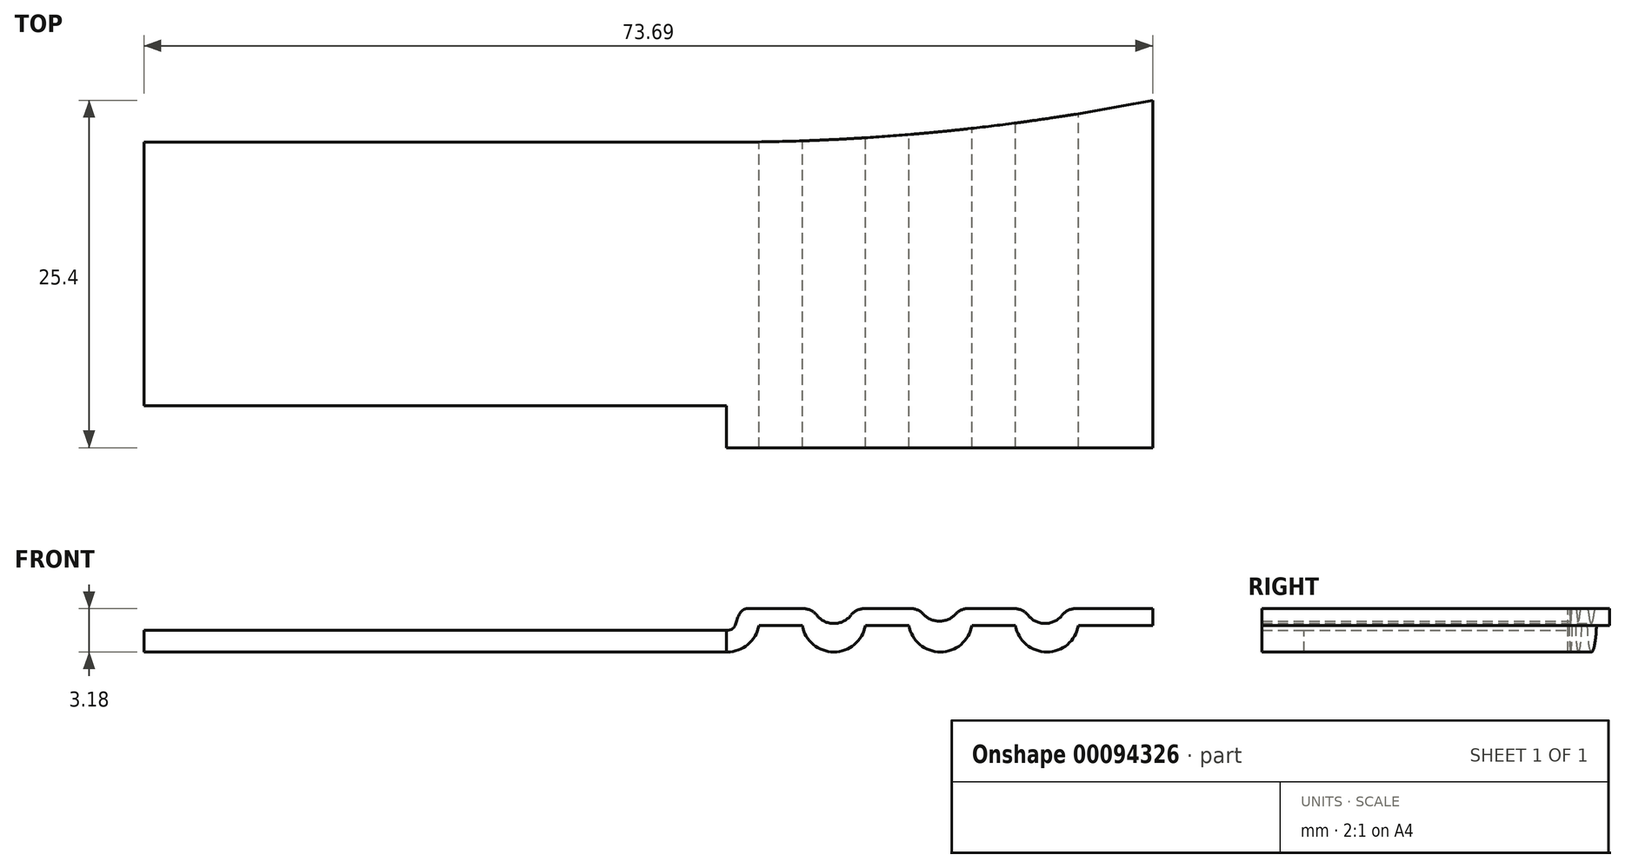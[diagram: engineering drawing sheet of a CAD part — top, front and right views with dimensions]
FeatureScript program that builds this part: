
annotation { "Feature Type Name" : "Feature", "Feature Type Description" : "" }
export const myFeature = defineFeature(function(context is Context, id is Id, definition is map)
    precondition{}
    {
        {
            var Q0;
            Q0=qCreatedBy(makeId("Front.planeOp"),FACE);
            var sketch = newSketch(context, id + "F0", { "sketchPlane" : qUnion([Q0])});
            skLineSegment(sketch, "E0", {"start": v(0, 0) * mm, "end": v(42.54, 0) * mm});
            skFitSpline(sketch, "E1", {"points": [v(42.55, 0) * mm, v(43.34, 0.8) * mm, v(44.13, 1.59) * mm], "startDerivative": vector(3.77, 0) * mm, "endDerivative": vector(2.62, 0) * mm});
            skLineSegment(sketch, "E2", {"start": v(44.13, 1.59) * mm, "end": v(48.9, 1.59) * mm});
            skPoint(sketch, "E3.1.internal.snap0", {"position": v(46.51, 1.59) * mm});
            skLineSegment(sketch, "E4", {"start": v(46.51, 1.59) * mm, "end": v(46.51, 4.58) * mm, "construction": true});
            skArc(sketch, "E5", {"start": v(48.9, 1.59) * mm, "mid": v(50.4, 0.5) * mm, "end": v(51.91, 1.59) * mm});
            skLineSegment(sketch, "E6", {"start": v(51.91, 1.59) * mm, "end": v(56.68, 1.59) * mm});
            skArc(sketch, "E7", {"start": v(56.68, 1.59) * mm, "mid": v(58.12, 0.66) * mm, "end": v(59.56, 1.59) * mm});
            skLineSegment(sketch, "E8", {"start": v(59.56, 1.59) * mm, "end": v(64.33, 1.59) * mm});
            skArc(sketch, "E9", {"start": v(64.33, 1.59) * mm, "mid": v(65.83, 0.5) * mm, "end": v(67.34, 1.59) * mm});
            skLineSegment(sketch, "E10", {"start": v(67.34, 1.59) * mm, "end": v(73.7, 1.59) * mm});
            skLineSegment(sketch, "E11", {"start": v(0, 0) * mm, "end": v(0, -1.59) * mm});
            skLineSegment(sketch, "E12", {"start": v(0, -1.59) * mm, "end": v(42.62, -1.59) * mm});
            skLineSegment(sketch, "E13", {"start": v(44.93, 0.35) * mm, "end": v(48.1, 0.35) * mm});
            skArc(sketch, "E14", {"start": v(42.62, -1.59) * mm, "mid": v(44.13, -1.04) * mm, "end": v(44.93, 0.35) * mm});
            skArc(sketch, "E15.MirrorCS", {"start": v(50.4, -1.59) * mm, "mid": v(48.9, -1.04) * mm, "end": v(48.1, 0.35) * mm});
            skLineSegment(sketch, "E16", {"start": v(54.3, 1.59) * mm, "end": v(54.3, 2.98) * mm, "construction": true});
            skLineSegment(sketch, "E17", {"start": v(61.94, 1.59) * mm, "end": v(61.94, 3.14) * mm, "construction": true});
            skArc(sketch, "E18", {"start": v(50.4, -1.59) * mm, "mid": v(51.9, -1.04) * mm, "end": v(52.7, 0.35) * mm});
            skLineSegment(sketch, "E19", {"start": v(52.7, 0.35) * mm, "end": v(55.88, 0.35) * mm});
            skArc(sketch, "E20.MirrorCS", {"start": v(58.19, -1.59) * mm, "mid": v(56.68, -1.04) * mm, "end": v(55.88, 0.35) * mm});
            skArc(sketch, "E21.MirrorCS", {"start": v(58.19, -1.59) * mm, "mid": v(59.7, -1.04) * mm, "end": v(60.49, 0.35) * mm});
            skLineSegment(sketch, "E22.MirrorCS", {"start": v(63.66, 0.35) * mm, "end": v(60.49, 0.35) * mm});
            skArc(sketch, "E23.MirrorCS", {"start": v(65.97, -1.59) * mm, "mid": v(64.46, -1.04) * mm, "end": v(63.66, 0.35) * mm});
            skPoint(sketch, "E24.endSnap0", {"position": v(65.83, 0.5) * mm});
            skLineSegment(sketch, "E25", {"start": v(65.97, -1.59) * mm, "end": v(65.97, -3.9) * mm, "construction": true});
            skArc(sketch, "E26.MirrorCS", {"start": v(65.97, -1.59) * mm, "mid": v(67.47, -1.04) * mm, "end": v(68.27, 0.35) * mm});
            skLineSegment(sketch, "E27", {"start": v(68.27, 0.35) * mm, "end": v(73.7, 0.35) * mm});
            skLineSegment(sketch, "E28", {"start": v(73.7, 0.35) * mm, "end": v(73.7, 1.59) * mm});
            skSolve(sketch);
        }
        {
            var Q0;
            Q0 = qSketchRegion(id + "F0", true);
            extrude(context, id + "F1", {"entities" : qUnion([Q0]), "depth" : 25.4 * mm});
        }
        {
            var Q0;
            Q0=makeQuery(id+"F1.opExtrude","SWEPT_FACE",FACE,{"disambiguationData":[OSD([sQuery(id+"F0.wireOp",EDGE,"E0")])]});
            var sketch = newSketch(context, id + "F2", { "sketchPlane" : qUnion([Q0])});
            skLineSegment(sketch, "E29", {"start": v(0, -12.7) * mm, "end": v(-12.15, -12.7) * mm, "construction": true});
            skLineSegment(sketch, "E30", {"start": v(0, -12.7) * mm, "end": v(0, -3.06) * mm});
            skLineSegment(sketch, "E31", {"start": v(0, -3.06) * mm, "end": v(42.55, -3.06) * mm});
            skArc(sketch, "E32", {"start": v(42.55, -3.06) * mm, "mid": v(58.2, -2.3) * mm, "end": v(73.7, 0) * mm});
            skLineSegment(sketch, "E33.MirrorCS", {"start": v(0, -12.7) * mm, "end": v(0, -22.34) * mm});
            skLineSegment(sketch, "E34.MirrorCS", {"start": v(0, -22.34) * mm, "end": v(42.55, -22.34) * mm});
            skArc(sketch, "E35.MirrorCS", {"start": v(42.55, -22.34) * mm, "mid": v(58.2, -23.1) * mm, "end": v(73.7, -25.4) * mm});
            skLineSegment(sketch, "E36", {"start": v(73.7, 0) * mm, "end": v(0, 0) * mm});
            skLineSegment(sketch, "E37", {"start": v(0, 0) * mm, "end": v(0, -3.06) * mm});
            skLineSegment(sketch, "E38", {"start": v(0, -22.34) * mm, "end": v(0, -25.4) * mm});
            skLineSegment(sketch, "E39", {"start": v(0, -25.4) * mm, "end": v(73.7, -25.4) * mm});
            skSolve(sketch);
        }
        {
            var Q0;
            {var subQ0=sQuery(id+"F2.wireOp",EDGE,"E31");Q0=makeQuery(id+"F2.imprint","IMPRINT",FACE,{"disambiguationData":[TD([[makeQuery(id+"F2.imprint","IMPRINT",EDGE,{"derivedFrom":subQ0}),1.0]])]});}
            var Q1;
            {var subQ0=sQuery(id+"F2.wireOp",EDGE,"E32");Q1=makeQuery(id+"F2.imprint","IMPRINT",FACE,{"disambiguationData":[TD([[makeQuery(id+"F2.imprint","IMPRINT",EDGE,{"derivedFrom":subQ0}),1.0]])]});}
            var Q2;
            {var subQ0=sQuery(id+"F2.wireOp",EDGE,"E34.MirrorCS");Q2=makeQuery(id+"F2.imprint","IMPRINT",FACE,{"disambiguationData":[TD([[makeQuery(id+"F2.imprint","IMPRINT",EDGE,{"derivedFrom":subQ0}),-1.0]])]});}
            var Q3;
            {var subQ0=sQuery(id+"F2.wireOp",EDGE,"E35.MirrorCS");Q3=makeQuery(id+"F2.imprint","IMPRINT",FACE,{"disambiguationData":[TD([[makeQuery(id+"F2.imprint","IMPRINT",EDGE,{"derivedFrom":subQ0}),-1.0]])]});}
            extrude(context, id + "F3", {"entities" : qUnion([Q0, Q1, Q2, Q3]), "operationType" : NewBodyOperationType.REMOVE, "endBound" : BoundingType.SYMMETRIC, "oppositeDirection" : true, "depth" : 25.4 * mm});
        }
        {
            var Q0;
            Q0=makeQuery(id+"F1.opExtrude","SWEPT_EDGE",EDGE,{"disambiguationData":[OSD([sQuery(id+"F0.wireOp",EDGE,"E2"),sQuery(id+"F0.wireOp",EDGE,"E5")])]});
            var Q1;
            Q1=makeQuery(id+"F1.opExtrude","SWEPT_EDGE",EDGE,{"disambiguationData":[OSD([sQuery(id+"F0.wireOp",EDGE,"E1"),sQuery(id+"F0.wireOp",EDGE,"E2")])]});
            var Q2;
            Q2=makeQuery(id+"F1.opExtrude","SWEPT_EDGE",EDGE,{"disambiguationData":[OSD([sQuery(id+"F0.wireOp",EDGE,"E5"),sQuery(id+"F0.wireOp",EDGE,"E6")])]});
            var Q3;
            Q3=makeQuery(id+"F1.opExtrude","SWEPT_EDGE",EDGE,{"disambiguationData":[OSD([sQuery(id+"F0.wireOp",EDGE,"E6"),sQuery(id+"F0.wireOp",EDGE,"E7")])]});
            var Q4;
            Q4=makeQuery(id+"F1.opExtrude","SWEPT_EDGE",EDGE,{"disambiguationData":[OSD([sQuery(id+"F0.wireOp",EDGE,"E7"),sQuery(id+"F0.wireOp",EDGE,"E8")])]});
            var Q5;
            Q5=makeQuery(id+"F1.opExtrude","SWEPT_EDGE",EDGE,{"disambiguationData":[OSD([sQuery(id+"F0.wireOp",EDGE,"E8"),sQuery(id+"F0.wireOp",EDGE,"E9")])]});
            var Q6;
            Q6=makeQuery(id+"F1.opExtrude","SWEPT_EDGE",EDGE,{"disambiguationData":[OSD([sQuery(id+"F0.wireOp",EDGE,"E9"),sQuery(id+"F0.wireOp",EDGE,"E10")])]});
            fillet(context, id + "F4", {"entities" : qUnion([Q0, Q1, Q2, Q3, Q4, Q5, Q6]), "radius" : 1.27 * mm, "tangentPropagation" : true, "allowEdgeOverflow" : false});
        }
    });
